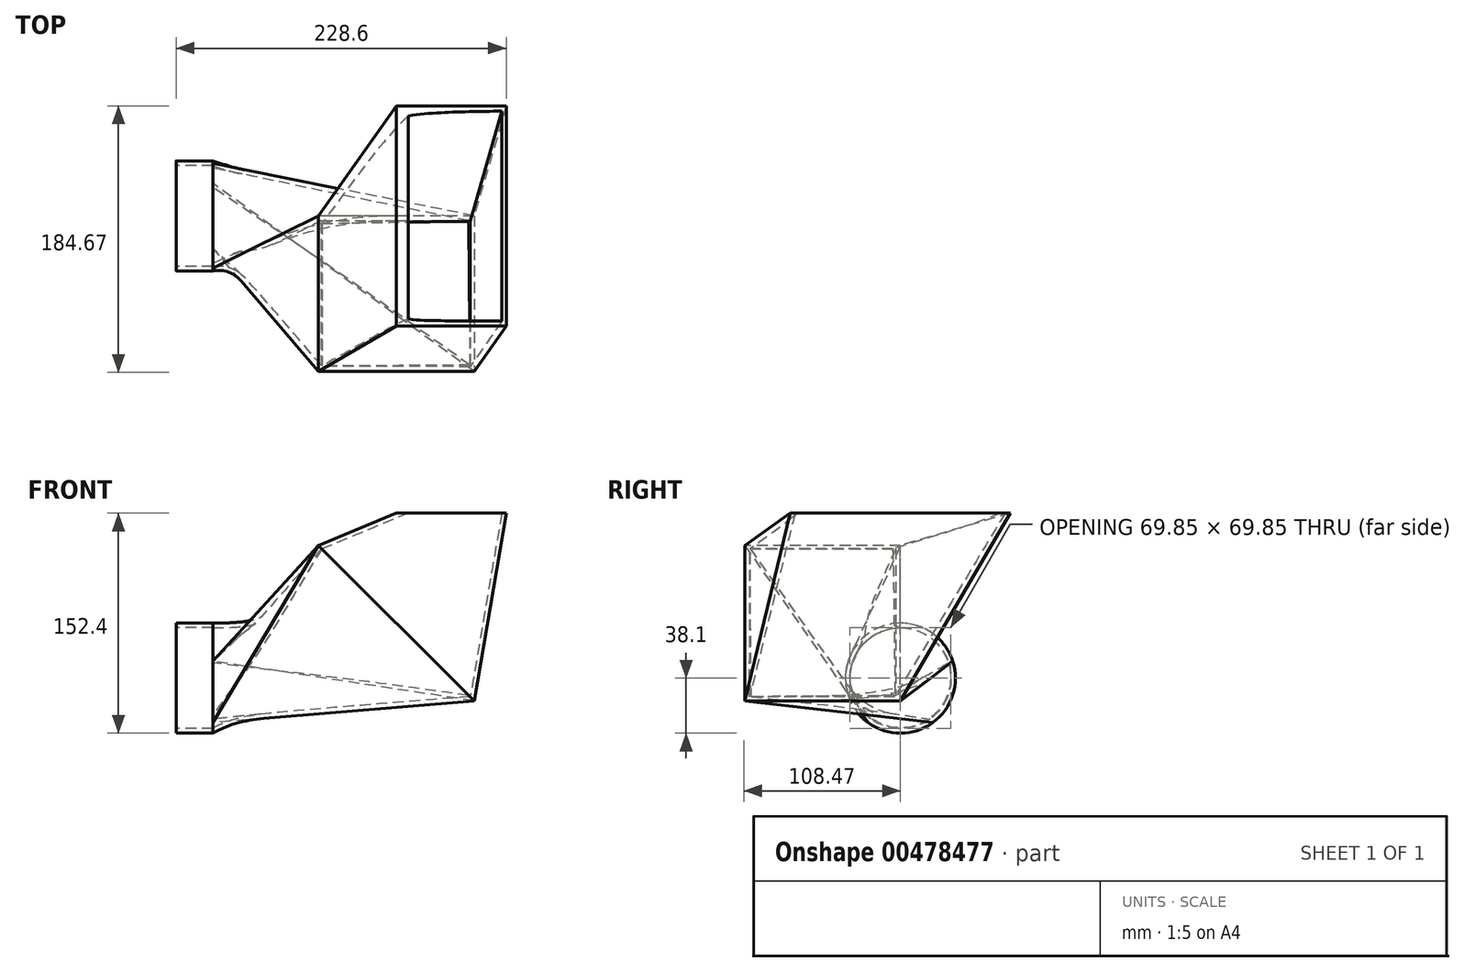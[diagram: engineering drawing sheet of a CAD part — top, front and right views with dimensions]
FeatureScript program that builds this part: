
annotation { "Feature Type Name" : "Feature", "Feature Type Description" : "" }
export const myFeature = defineFeature(function(context is Context, id is Id, definition is map)
    precondition{}
    {
        {
            var Q0;
            Q0=qCreatedBy(makeId("Front.planeOp"),FACE);
            var sketch = newSketch(context, id + "F0", { "sketchPlane" : qUnion([Q0])});
            skLineSegment(sketch, "E0", {"start": v(0, 76.2) * mm, "end": v(0, 0) * mm});
            skLineSegment(sketch, "E1", {"start": v(0, 0) * mm, "end": v(-127, 0) * mm});
            skLineSegment(sketch, "E2", {"start": v(-127, 0) * mm, "end": v(-152.4, 0) * mm});
            skLineSegment(sketch, "E3", {"start": v(76.2, 76.2) * mm, "end": v(0, 0) * mm});
            skSolve(sketch);
        }
        {
            var Q0;
            Q0=sQuery(id+"F0.wireOp",VERTEX,"E0.start");
            var Q1;
            Q1=sQuery(id+"F0.wireOp",EDGE,"E0");
            cPlane(context, id + "F1", {"entities" : qUnion([Q0, Q1]), "cplaneType" : CPlaneType.LINE_POINT, "offset" : 25.4 * mm, "width" : 152.4 * mm, "height" : 152.4 * mm});
        }
        {
            var Q0;
            Q0=sQuery(id+"F0.wireOp",EDGE,"E3");
            var Q1;
            Q1=sQuery(id+"F0.wireOp",VERTEX,"E1.start");
            cPlane(context, id + "F2", {"entities" : qUnion([Q0, Q1]), "cplaneType" : CPlaneType.LINE_POINT, "offset" : 25.4 * mm, "width" : 152.4 * mm, "height" : 152.4 * mm});
        }
        {
            var Q0;
            Q0=sQuery(id+"F0.wireOp",VERTEX,"E2.start");
            var Q1;
            Q1=qCreatedBy(makeId("Right.planeOp"),FACE);
            cPlane(context, id + "F3", {"entities" : qUnion([Q0, Q1]), "cplaneType" : CPlaneType.PLANE_POINT, "offset" : 25.4 * mm, "width" : 152.4 * mm, "height" : 152.4 * mm});
        }
        {
            var Q0;
            Q0=sQuery(id+"F0.wireOp",VERTEX,"E2.end");
            var Q1;
            Q1=qCreatedBy(id+"F3.planeOp",FACE);
            cPlane(context, id + "F4", {"entities" : qUnion([Q0, Q1]), "cplaneType" : CPlaneType.PLANE_POINT, "offset" : 25.4 * mm, "width" : 152.4 * mm, "height" : 152.4 * mm});
        }
        {
            var Q0;
            Q0=qCreatedBy(id+"F1.planeOp",FACE);
            var sketch = newSketch(context, id + "F5", { "sketchPlane" : qUnion([Q0])});
            skLineSegment(sketch, "E4.bottom", {"start": v(0, -76.2) * mm, "end": v(76.2, -76.2) * mm});
            skLineSegment(sketch, "E4.top", {"start": v(0, 76.2) * mm, "end": v(76.2, 76.2) * mm});
            skLineSegment(sketch, "E4.left", {"start": v(0, -76.2) * mm, "end": v(0, 76.2) * mm});
            skLineSegment(sketch, "E4.right", {"start": v(76.2, -76.2) * mm, "end": v(76.2, 76.2) * mm});
            skSolve(sketch);
        }
        {
            var Q0;
            Q0=qCreatedBy(id+"F2.planeOp",FACE);
            var sketch = newSketch(context, id + "F6", { "sketchPlane" : qUnion([Q0])});
            skLineSegment(sketch, "E5.bottom", {"start": v(0, -76.2) * mm, "end": v(107.76, -76.2) * mm});
            skLineSegment(sketch, "E5.top", {"start": v(0, 76.2) * mm, "end": v(107.76, 76.2) * mm});
            skLineSegment(sketch, "E5.left", {"start": v(0, -76.2) * mm, "end": v(0, 76.2) * mm});
            skLineSegment(sketch, "E5.right", {"start": v(107.76, -76.2) * mm, "end": v(107.76, 76.2) * mm});
            skSolve(sketch);
        }
        {
            var Q0;
            Q0=qCreatedBy(id+"F3.planeOp",FACE);
            var sketch = newSketch(context, id + "F7", { "sketchPlane" : qUnion([Q0])});
            skCircle(sketch, "E6", {"center": v(0, -38.1) * mm, "radius": 38.1 * mm});
            skSolve(sketch);
        }
        {
            var Q0;
            Q0=makeQuery(id+"F5.imprint","IMPRINT",FACE,{"disambiguationData":[TD([[makeQuery(id+"F5.imprint","IMPRINT",EDGE,{"derivedFrom":sQuery(id+"F5.wireOp",EDGE,"E4.bottom")}),1.0]])]});
            var Q1;
            Q1=makeQuery(id+"F6.imprint","IMPRINT",FACE,{"disambiguationData":[TD([[makeQuery(id+"F6.imprint","IMPRINT",EDGE,{"derivedFrom":sQuery(id+"F6.wireOp",EDGE,"E5.bottom")}),1.0]])]});
            loft(context, id + "F8", {"sheetProfilesArray" : [{ "sheetProfileEntities" : qUnion([Q0]) }, { "sheetProfileEntities" : qUnion([Q1]) }]});
        }
        {
            var Q1;
            Q1=makeQuery(id+"F8.opLoft","CAP_FACE",FACE,{"disambiguationData":[OSD([makeQuery(id+"F6.imprint","IMPRINT",FACE,{"disambiguationData":[TD([[makeQuery(id+"F6.imprint","IMPRINT",EDGE,{"derivedFrom":sQuery(id+"F6.wireOp",EDGE,"E5.bottom")}),1.0]])]})])],"isStart":true});
            var Q2;
            Q2=makeQuery(id+"F7.imprint","IMPRINT",FACE,{"disambiguationData":[TD([[makeQuery(id+"F7.imprint","IMPRINT",EDGE,{"derivedFrom":sQuery(id+"F7.wireOp",EDGE,"E6")}),1.0]])]});
            var Q3;
            Q3=sQuery(id+"F0.wireOp",EDGE,"E1");
            loft(context, id + "F9", {"addGuides" : true, "sheetProfilesArray" : [{ "sheetProfileEntities" : qUnion([Q1]) }, { "sheetProfileEntities" : qUnion([Q2]) }], "guidesArray" : [{ "guideEntities" : qUnion([Q3]), "guideDerivativeType" : LoftGuideDerivativeType.DEFAULT, "guideDerivativeMagnitude" : 1 }]});
        }
        {
            var Q0;
            Q0=makeQuery(id+"F9.opLoft","CAP_FACE",FACE,{"disambiguationData":[OSD([makeQuery(id+"F7.imprint","IMPRINT",FACE,{"disambiguationData":[TD([[makeQuery(id+"F7.imprint","IMPRINT",EDGE,{"derivedFrom":sQuery(id+"F7.wireOp",EDGE,"E6")}),1.0]])]})])],"isStart":true});
            var Q1;
            Q1=qCreatedBy(id+"F4.planeOp",FACE);
            extrude(context, id + "F10", {"entities" : qUnion([Q0]), "endBound" : BoundingType.UP_TO_SURFACE, "endBoundEntityFace" : qUnion([Q1]), "depth" : 25.4 * mm});
        }
        {
            var Q0;
            Q0=makeQuery(id+"F8.opLoft","CAP_FACE",FACE,{"disambiguationData":[OSD([makeQuery(id+"F5.imprint","IMPRINT",FACE,{"disambiguationData":[TD([[makeQuery(id+"F5.imprint","IMPRINT",EDGE,{"derivedFrom":sQuery(id+"F5.wireOp",EDGE,"E4.bottom")}),1.0]])]})])],"isStart":true});
            var Q1;
            Q1=makeQuery(id+"F8.opLoft","CAP_FACE",FACE,{"disambiguationData":[OSD([makeQuery(id+"F6.imprint","IMPRINT",FACE,{"disambiguationData":[TD([[makeQuery(id+"F6.imprint","IMPRINT",EDGE,{"derivedFrom":sQuery(id+"F6.wireOp",EDGE,"E5.bottom")}),1.0]])]})])],"isStart":true});
            var Q2;
            Q2=makeQuery(id+"F9.opLoft","CAP_FACE",FACE,{"disambiguationData":[OSD([makeQuery(id+"F6.imprint","IMPRINT",FACE,{"disambiguationData":[TD([[makeQuery(id+"F6.imprint","IMPRINT",EDGE,{"derivedFrom":sQuery(id+"F6.wireOp",EDGE,"E5.bottom")}),1.0]])]})])],"isStart":true});
            var Q3;
            Q3=makeQuery(id+"F9.opLoft","CAP_FACE",FACE,{"disambiguationData":[OSD([makeQuery(id+"F7.imprint","IMPRINT",FACE,{"disambiguationData":[TD([[makeQuery(id+"F7.imprint","IMPRINT",EDGE,{"derivedFrom":sQuery(id+"F7.wireOp",EDGE,"E6")}),1.0]])]})])],"isStart":true});
            var Q4;
            Q4=makeQuery(id+"F10.opExtrude","CAP_FACE",FACE,{"disambiguationData":[OSD([makeQuery(id+"F7.imprint","IMPRINT",FACE,{"disambiguationData":[TD([[makeQuery(id+"F7.imprint","IMPRINT",EDGE,{"derivedFrom":sQuery(id+"F7.wireOp",EDGE,"E6")}),1.0]])]})])],"isStart":false});
            var Q5;
            Q5=makeQuery(id+"F10.opExtrude","CAP_FACE",FACE,{"disambiguationData":[OSD([makeQuery(id+"F7.imprint","IMPRINT",FACE,{"disambiguationData":[TD([[makeQuery(id+"F7.imprint","IMPRINT",EDGE,{"derivedFrom":sQuery(id+"F7.wireOp",EDGE,"E6")}),1.0]])]})])],"isStart":true});
            var Q6;
            Q6=makeQuery(id+"F10.opExtrude","CAP_FACE",FACE,{"disambiguationData":[OSD([makeQuery(id+"F7.imprint","IMPRINT",FACE,{"disambiguationData":[TD([[makeQuery(id+"F7.imprint","IMPRINT",EDGE,{"derivedFrom":sQuery(id+"F7.wireOp",EDGE,"E6")}),1.0]])]})])],"isStart":false});
            shell(context, id + "F11", {"entities" : qUnion([Q0, Q1, Q2, Q3, Q4, Q5, Q6]), "thickness" : 3.17 * mm});
        }
    });
